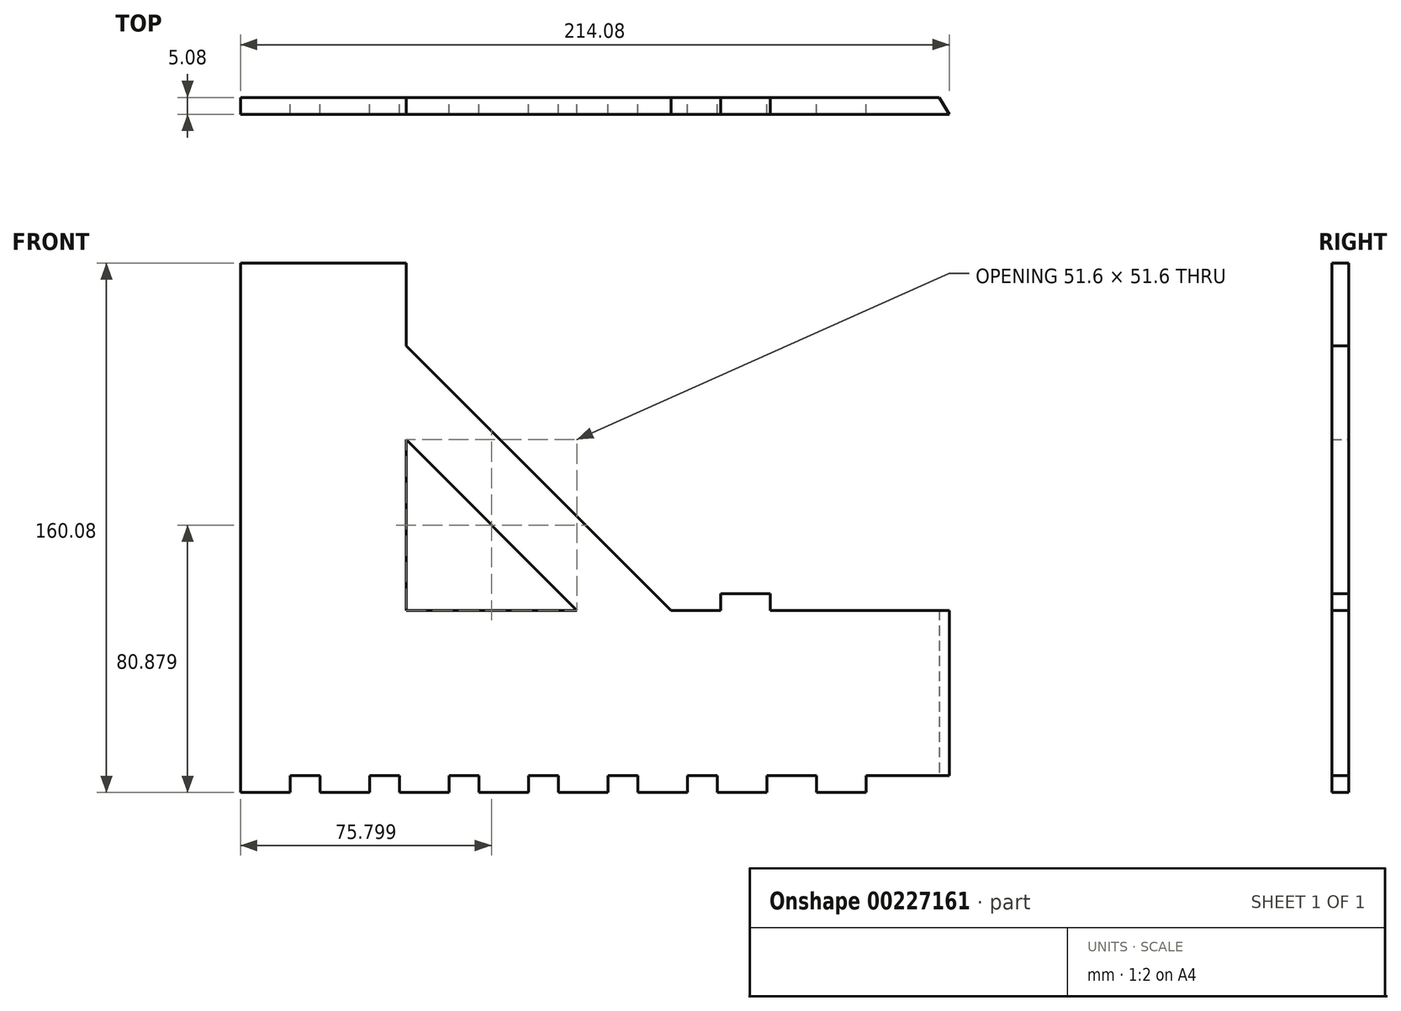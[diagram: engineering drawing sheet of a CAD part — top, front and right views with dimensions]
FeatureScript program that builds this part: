
annotation { "Feature Type Name" : "Feature", "Feature Type Description" : "" }
export const myFeature = defineFeature(function(context is Context, id is Id, definition is map)
    precondition{}
    {
        {
            var Q0;
            Q0=qCreatedBy(makeId("Front.planeOp"),FACE);
            var sketch = newSketch(context, id + "F0", { "sketchPlane" : qUnion([Q0])});
            skLineSegment(sketch, "E0", {"start": v(-32.42, 0) * mm, "end": v(-246.5, 0) * mm});
            skLineSegment(sketch, "E1", {"start": v(-246.5, 0) * mm, "end": v(-246.5, 130) * mm});
            skLineSegment(sketch, "E2", {"start": v(-246.5, 130) * mm, "end": v(-196.5, 130) * mm});
            skLineSegment(sketch, "E3", {"start": v(-196.5, 130) * mm, "end": v(-196.5, 50) * mm});
            skLineSegment(sketch, "E4", {"start": v(-196.5, 50) * mm, "end": v(-32.42, 50) * mm});
            skLineSegment(sketch, "E5", {"start": v(-196.5, 130) * mm, "end": v(-116.5, 50) * mm});
            skLineSegment(sketch, "E6", {"start": v(-196.5, 101.6) * mm, "end": v(-144.9, 50) * mm});
            skLineSegment(sketch, "E7", {"start": v(-246.5, 0) * mm, "end": v(-246.5, -5.08) * mm});
            skLineSegment(sketch, "E8", {"start": v(-246.5, -5.08) * mm, "end": v(-231.5, -5.08) * mm});
            skLineSegment(sketch, "E9", {"start": v(-231.5, -5.08) * mm, "end": v(-231.5, 0) * mm});
            skLineSegment(sketch, "E10.1.0.0", {"start": v(-207.5, -5.08) * mm, "end": v(-207.5, 0) * mm});
            skLineSegment(sketch, "E10.1.0.1", {"start": v(-222.5, -5.08) * mm, "end": v(-207.5, -5.08) * mm});
            skLineSegment(sketch, "E10.1.0.2", {"start": v(-222.5, 0) * mm, "end": v(-222.5, -5.08) * mm});
            skLineSegment(sketch, "E10.2.0.0", {"start": v(-183.5, -5.08) * mm, "end": v(-183.5, 0) * mm});
            skLineSegment(sketch, "E10.2.0.1", {"start": v(-198.5, -5.08) * mm, "end": v(-183.5, -5.08) * mm});
            skLineSegment(sketch, "E10.2.0.2", {"start": v(-198.5, 0) * mm, "end": v(-198.5, -5.08) * mm});
            skLineSegment(sketch, "E10.3.0.0", {"start": v(-159.5, -5.08) * mm, "end": v(-159.5, 0) * mm});
            skLineSegment(sketch, "E10.3.0.1", {"start": v(-174.5, -5.08) * mm, "end": v(-159.5, -5.08) * mm});
            skLineSegment(sketch, "E10.3.0.2", {"start": v(-174.5, 0) * mm, "end": v(-174.5, -5.08) * mm});
            skLineSegment(sketch, "E10.4.0.0", {"start": v(-135.5, -5.08) * mm, "end": v(-135.5, 0) * mm});
            skLineSegment(sketch, "E10.4.0.1", {"start": v(-150.5, -5.08) * mm, "end": v(-135.5, -5.08) * mm});
            skLineSegment(sketch, "E10.4.0.2", {"start": v(-150.5, 0) * mm, "end": v(-150.5, -5.08) * mm});
            skLineSegment(sketch, "E10.5.0.0", {"start": v(-111.5, -5.08) * mm, "end": v(-111.5, 0) * mm});
            skLineSegment(sketch, "E10.5.0.1", {"start": v(-126.5, -5.08) * mm, "end": v(-111.5, -5.08) * mm});
            skLineSegment(sketch, "E10.5.0.2", {"start": v(-126.5, 0) * mm, "end": v(-126.5, -5.08) * mm});
            skLineSegment(sketch, "E10.6.0.0", {"start": v(-87.5, -5.08) * mm, "end": v(-87.5, 0) * mm});
            skLineSegment(sketch, "E10.6.0.1", {"start": v(-102.5, -5.08) * mm, "end": v(-87.5, -5.08) * mm});
            skLineSegment(sketch, "E10.6.0.2", {"start": v(-102.5, 0) * mm, "end": v(-102.5, -5.08) * mm});
            skLineSegment(sketch, "E10.direction1", {"start": v(-246.5, -5.08) * mm, "end": v(-222.5, -5.08) * mm, "construction": true});
            skLineSegment(sketch, "E11", {"start": v(-32.42, 50) * mm, "end": v(-32.42, 0) * mm});
            skPoint(sketch, "E12.start.orphan", {"position": v(0, 50) * mm});
            skSolve(sketch);
        }
        {
            var Q0;
            Q0=qSketchRegion(id+"F0",true);
            extrude(context, id + "F1", {"entities" : qUnion([Q0]), "depth" : 5.08 * mm});
        }
        {
            var Q0;
            Q0=makeQuery(id+"F1.opExtrude","SWEPT_FACE",FACE,{"disambiguationData":[OSD([sQuery(id+"F0.wireOp",EDGE,"E2")])]});
            var Q1;
            Q1=makeQuery(id+"F1.opExtrude","SWEPT_FACE",FACE,{"disambiguationData":[OSD([sQuery(id+"F0.wireOp",EDGE,"0f3f7d79-0024-4810-854d-b7a6c9fa19c64.MirrorCS")])]});
            extrude(context, id + "F2", {"entities" : qUnion([Q0, Q1]), "operationType" : NewBodyOperationType.ADD, "depth" : 25 * mm});
        }
        {
            var Q0;
            {var subQ0=sQuery(id+"F0.wireOp",EDGE,"E0");Q0=makeQuery(id+"F1.opExtrude","SWEPT_FACE",FACE,{"disambiguationData":[OSD([subQ0]),TDD([makeQuery(id+"F0.imprint","IMPRINT",EDGE,{"disambiguationData":[TD([[makeQuery(id+"F0.imprint","INTERSECT",VERTEX,{"derivedFrom":[subQ0,sQuery(id+"F0.wireOp",EDGE,"E11")]}),-1.0]])],"derivedFrom":subQ0})])]});}
            var sketch = newSketch(context, id + "F3", { "sketchPlane" : qUnion([Q0])});
            skLineSegment(sketch, "E13", {"start": v(-32.42, 5.08) * mm, "end": v(-35.35, 0) * mm});
            skSolve(sketch);
        }
        {
            var Q0;
            {var subQ0=sQuery(id+"F3.wireOp",EDGE,"E13");Q0=makeQuery(id+"F3.imprint","IMPRINT",FACE,{"disambiguationData":[TD([[makeQuery(id+"F3.imprint","IMPRINT",EDGE,{"derivedFrom":subQ0}),1.0]])]});}
            extrude(context, id + "F4", {"entities" : qUnion([Q0]), "operationType" : NewBodyOperationType.REMOVE, "oppositeDirection" : true, "depth" : 58 * mm});
        }
        {
            var Q0;
            {var subQ0=sQuery(id+"F0.wireOp",EDGE,"E0");Q0=makeQuery(id+"F1.opExtrude","SWEPT_FACE",FACE,{"disambiguationData":[OSD([subQ0]),TDD([makeQuery(id+"F0.imprint","IMPRINT",EDGE,{"disambiguationData":[TD([[makeQuery(id+"F0.imprint","INTERSECT",VERTEX,{"derivedFrom":[subQ0,sQuery(id+"F0.wireOp",EDGE,"E11")]}),-1.0]])],"derivedFrom":subQ0})])]});}
            var sketch = newSketch(context, id + "F5", { "sketchPlane" : qUnion([Q0])});
            skLineSegment(sketch, "E14.bottom", {"start": v(-72.5, 5.08) * mm, "end": v(-57.5, 5.08) * mm});
            skLineSegment(sketch, "E14.top", {"start": v(-72.5, 0) * mm, "end": v(-57.5, 0) * mm});
            skLineSegment(sketch, "E14.right", {"start": v(-57.5, 5.08) * mm, "end": v(-57.5, 0) * mm});
            skLineSegment(sketch, "E15", {"start": v(-72.5, 5.08) * mm, "end": v(-72.5, 0) * mm});
            skPoint(sketch, "E14.left.start.orphan", {"position": v(-87.5, 5.08) * mm});
            skPoint(sketch, "E16.orphan", {"position": v(-87.5, 0) * mm});
            skSolve(sketch);
        }
        {
            var Q0;
            Q0 = qSketchRegion(id + "F5", true);
            extrude(context, id + "F6", {"entities" : qUnion([Q0]), "operationType" : NewBodyOperationType.ADD, "depth" : 5.08 * mm});
        }
        {
            var Q0;
            {var subQ0=sQuery(id+"F0.wireOp",EDGE,"E4");Q0=makeQuery(id+"F1.opExtrude","SWEPT_FACE",FACE,{"disambiguationData":[OSD([subQ0]),TDD([makeQuery(id+"F0.imprint","IMPRINT",EDGE,{"disambiguationData":[TD([[makeQuery(id+"F0.imprint","INTERSECT",VERTEX,{"derivedFrom":[subQ0,sQuery(id+"F0.wireOp",EDGE,"E11")]}),1.0]])],"derivedFrom":subQ0})])]});}
            var sketch = newSketch(context, id + "F7", { "sketchPlane" : qUnion([Q0])});
            skLineSegment(sketch, "E17.bottom", {"start": v(-101.5, 0) * mm, "end": v(-86.5, 0) * mm});
            skLineSegment(sketch, "E17.top", {"start": v(-101.5, -5.08) * mm, "end": v(-86.5, -5.08) * mm});
            skLineSegment(sketch, "E17.right", {"start": v(-86.5, 0) * mm, "end": v(-86.5, -5.08) * mm});
            skLineSegment(sketch, "E18", {"start": v(-101.5, 0) * mm, "end": v(-101.5, -5.08) * mm});
            skPoint(sketch, "E17.left.start.orphan", {"position": v(-116.5, 0) * mm});
            skPoint(sketch, "E19.orphan", {"position": v(-116.5, -5.08) * mm});
            skSolve(sketch);
        }
        {
            var Q0;
            Q0 = qSketchRegion(id + "F7", true);
            extrude(context, id + "F8", {"entities" : qUnion([Q0]), "operationType" : NewBodyOperationType.ADD, "depth" : 5.08 * mm});
        }
    });
